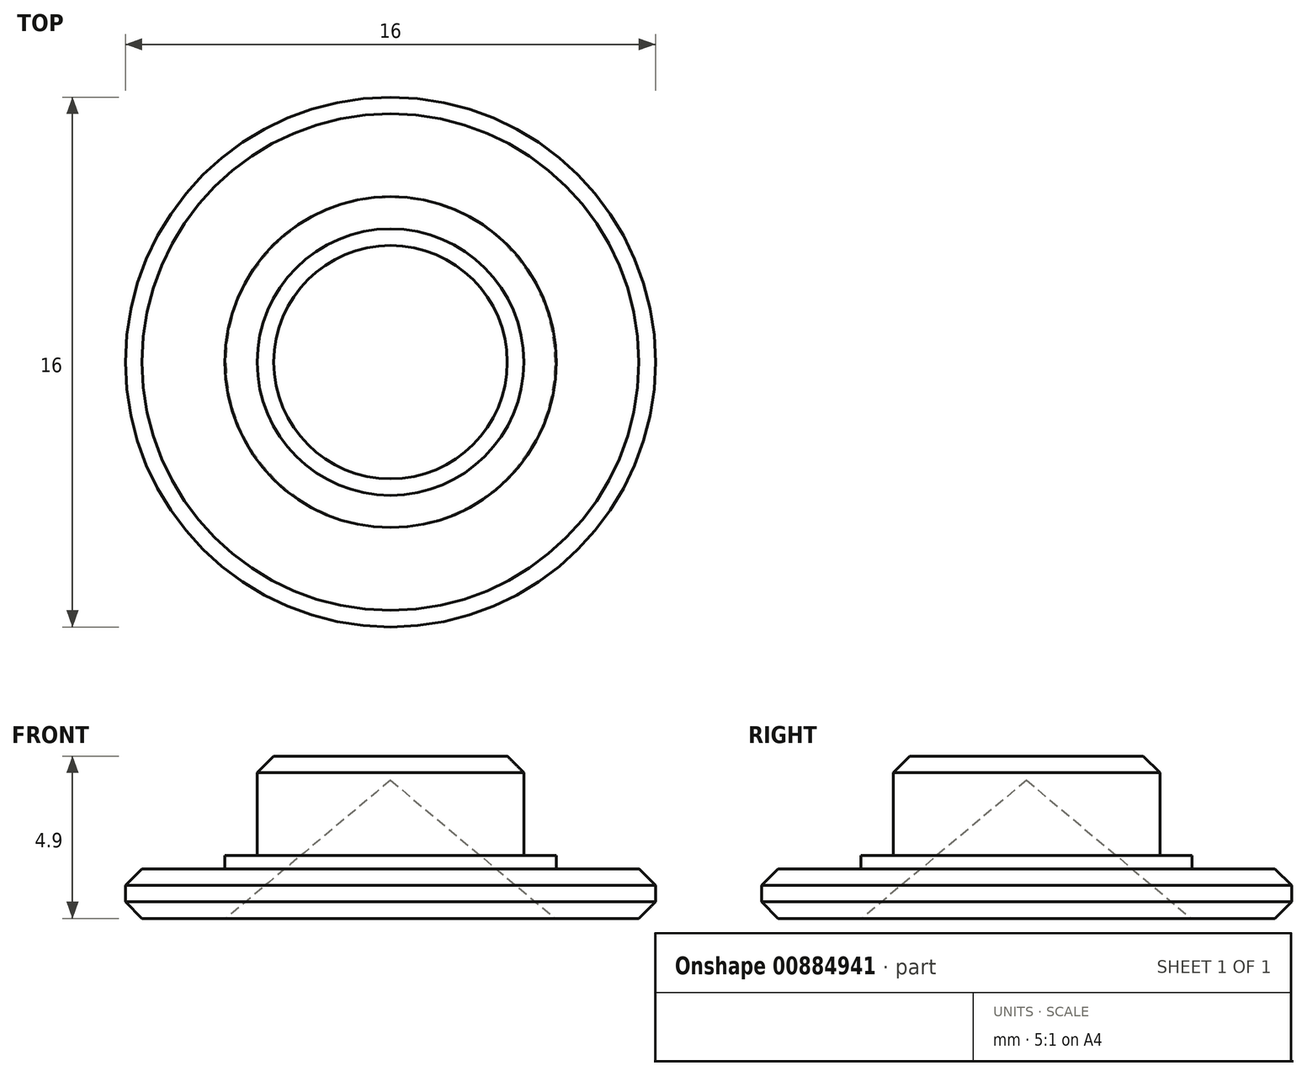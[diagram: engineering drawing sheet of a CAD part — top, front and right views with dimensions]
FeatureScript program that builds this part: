
annotation { "Feature Type Name" : "Feature", "Feature Type Description" : "" }
export const myFeature = defineFeature(function(context is Context, id is Id, definition is map)
    precondition{}
    {
        {
            var Q0;
            Q0=qCreatedBy(makeId("Top.planeOp"),FACE);
            var sketch = newSketch(context, id + "F0", { "sketchPlane" : qUnion([Q0])});
            skCircle(sketch, "E0", {"center": v(0, 0) * mm, "radius": 8 * mm});
            skSolve(sketch);
        }
        {
            var Q0;
            Q0=qSketchRegion(id+"F0",true);
            extrude(context, id + "F1", {"entities" : qUnion([Q0]), "depth" : 1.5 * mm, "offsetDistance" : 25 * mm});
        }
        {
            var Q0;
            Q0=makeQuery(id+"F1.opExtrude","CAP_FACE",FACE,{"disambiguationData":[OSD([sQuery(id+"F0.wireOp",EDGE,"E0")])],"isStart":false});
            var sketch = newSketch(context, id + "F2", { "sketchPlane" : qUnion([Q0])});
            skCircle(sketch, "E1", {"center": v(0, 0) * mm, "radius": 5 * mm});
            skSolve(sketch);
        }
        {
            var Q0;
            Q0=qSketchRegion(id+"F2",true);
            extrude(context, id + "F3", {"entities" : qUnion([Q0]), "operationType" : NewBodyOperationType.ADD, "depth" : 0.4 * mm, "offsetDistance" : 25 * mm});
        }
        {
            var Q0;
            Q0=makeQuery(id+"F3.opExtrude","CAP_FACE",FACE,{"disambiguationData":[OSD([sQuery(id+"F2.wireOp",EDGE,"E1")])],"isStart":false});
            var sketch = newSketch(context, id + "F4", { "sketchPlane" : qUnion([Q0])});
            skCircle(sketch, "E2", {"center": v(0, 0) * mm, "radius": 4.03 * mm});
            skSolve(sketch);
        }
        {
            var Q0;
            Q0=qSketchRegion(id+"F4",true);
            extrude(context, id + "F5", {"entities" : qUnion([Q0]), "operationType" : NewBodyOperationType.ADD, "depth" : 3 * mm, "offsetDistance" : 25 * mm});
        }
        {
            var Q0;
            Q0=makeQuery(id+"F1.opExtrude","CAP_EDGE",EDGE,{"disambiguationData":[OSD([sQuery(id+"F0.wireOp",EDGE,"E0")])],"isStart":true});
            var Q1;
            Q1=makeQuery(id+"F1.opExtrude","CAP_EDGE",EDGE,{"disambiguationData":[OSD([sQuery(id+"F0.wireOp",EDGE,"E0")])],"isStart":false});
            var Q2;
            Q2=makeQuery(id+"F5.opExtrude","CAP_EDGE",EDGE,{"disambiguationData":[OSD([sQuery(id+"F4.wireOp",EDGE,"E2")])],"isStart":false});
            chamfer(context, id + "F6", {"entities" : qUnion([Q0, Q1, Q2]), "width" : 0.5 * mm, "tangentPropagation" : true});
        }
        {
            var Q0;
            Q0=qCreatedBy(makeId("Front.planeOp"),FACE);
            var sketch = newSketch(context, id + "F7", { "sketchPlane" : qUnion([Q0])});
            skLineSegment(sketch, "E3", {"start": v(-4.97, 0) * mm, "end": v(0, 4.17) * mm});
            skLineSegment(sketch, "E4", {"start": v(0, 4.17) * mm, "end": v(0, 0) * mm});
            skLineSegment(sketch, "E5", {"start": v(0, 0) * mm, "end": v(-4.97, 0) * mm});
            skSolve(sketch);
        }
        {
            var Q0;
            Q0=qSketchRegion(id+"F7",true);
            var Q1;
            Q1=sQuery(id+"F7.wireOp",EDGE,"E4");
            revolve(context, id + "F8", {"operationType" : NewBodyOperationType.REMOVE, "entities" : qUnion([Q0]), "axis" : qUnion([Q1]), "revolveType" : RevolveType.FULL, "oppositeDirection" : true});
        }
    });
